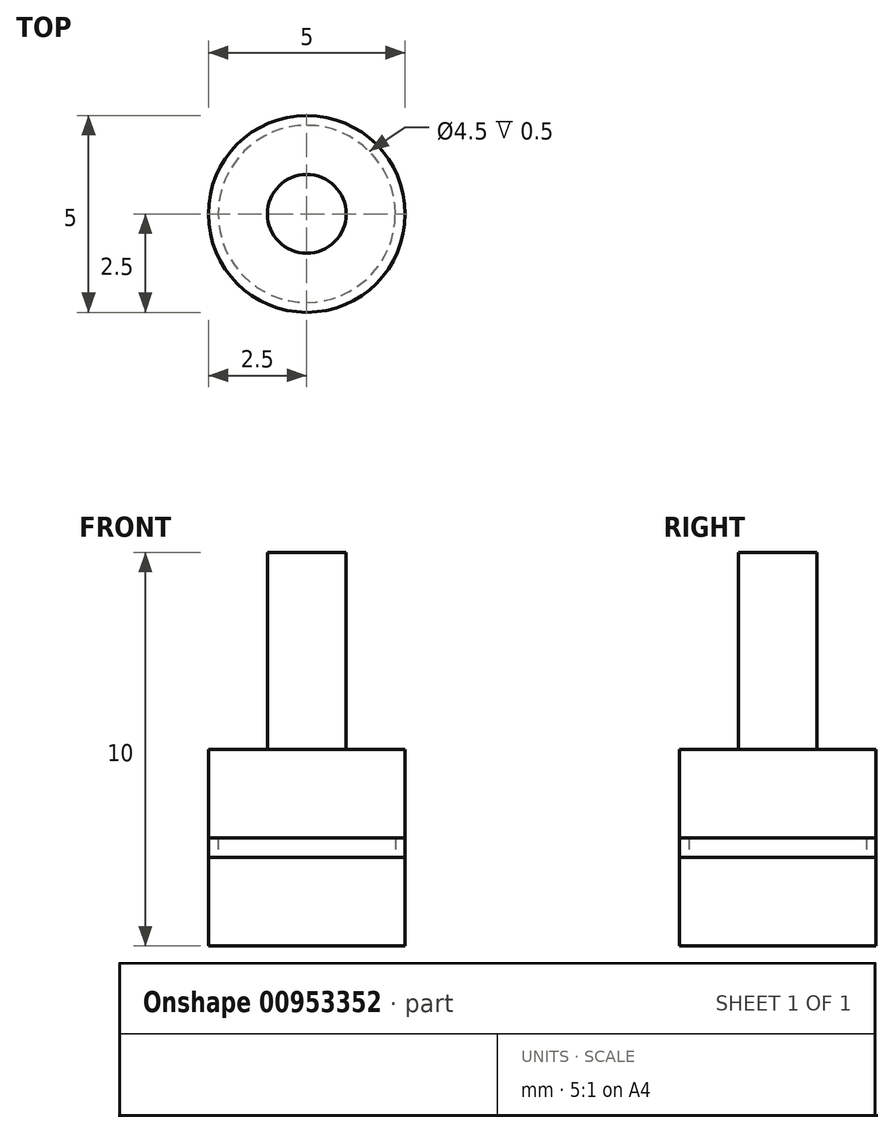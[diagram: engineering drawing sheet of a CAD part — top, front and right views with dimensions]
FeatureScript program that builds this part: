
annotation { "Feature Type Name" : "Feature", "Feature Type Description" : "" }
export const myFeature = defineFeature(function(context is Context, id is Id, definition is map)
    precondition{}
    {
        {
            var Q0;
            Q0=qCreatedBy(makeId("Top.planeOp"),FACE);
            var sketch = newSketch(context, id + "F0", { "sketchPlane" : qUnion([Q0])});
            skCircle(sketch, "E0", {"center": v(0, 0) * mm, "radius": 2.5 * mm});
            skSolve(sketch);
        }
        {
            var Q0;
            Q0=qSketchRegion(id+"F0",true);
            extrude(context, id + "F1", {"entities" : qUnion([Q0]), "depth" : 5 * mm, "offsetDistance" : 25 * mm});
        }
        {
            var Q0;
            Q0=makeQuery(id+"F1.opExtrude","CAP_FACE",FACE,{"disambiguationData":[OSD([sQuery(id+"F0.wireOp",EDGE,"E0")])],"isStart":false});
            cPlane(context, id + "F2", {"entities" : qUnion([Q0]), "cplaneType" : CPlaneType.OFFSET, "offset" : 2.5 * mm, "oppositeDirection" : true, "width" : 150 * mm, "height" : 150 * mm});
        }
        {
            var Q0;
            Q0=makeQuery(id+"F1.opExtrude","CAP_FACE",FACE,{"disambiguationData":[OSD([sQuery(id+"F0.wireOp",EDGE,"E0")])],"isStart":false});
            var sketch = newSketch(context, id + "F3", { "sketchPlane" : qUnion([Q0])});
            skCircle(sketch, "E1", {"center": v(0, 0) * mm, "radius": 1 * mm});
            skSolve(sketch);
        }
        {
            var Q0;
            Q0=qSketchRegion(id+"F3",true);
            extrude(context, id + "F4", {"entities" : qUnion([Q0]), "operationType" : NewBodyOperationType.ADD, "depth" : 5 * mm, "offsetDistance" : 25 * mm});
        }
        {
            var Q0;
            Q0=qCreatedBy(id+"F2.planeOp",FACE);
            var sketch = newSketch(context, id + "F5", { "sketchPlane" : qUnion([Q0])});
            skCircle(sketch, "E2", {"center": v(0, 0) * mm, "radius": 2.5 * mm});
            skCircle(sketch, "E3.0", {"center": v(0, 0) * mm, "radius": 2.25 * mm});
            skSolve(sketch);
        }
        {
            var Q0;
            Q0=qSketchRegion(id+"F5",true);
            extrude(context, id + "F6", {"entities" : qUnion([Q0]), "operationType" : NewBodyOperationType.REMOVE, "endBound" : BoundingType.SYMMETRIC, "depth" : .5 * mm, "offsetDistance" : 25 * mm});
        }
        {
            var Q0;
            Q0=qSketchRegion(id+"F5",true);
            extrude(context, id + "F7", {"entities" : qUnion([Q0]), "endBound" : BoundingType.SYMMETRIC, "depth" : .5 * mm, "offsetDistance" : 25 * mm});
        }
    });
